# Revit family: Gira_537303
name_source: partatom
category: Electrical Fixtures
revit_build: Autodesk Revit 2017 (Build: 20160225_1515(x64)
units: mm (PartAtom-declared; Revit-internal decimal feet)

## family parameters
Cut with Voids When Loaded = No
Host = Face
Maintain Annotation Orientation = Yes
Part Type = Normal
Room Calculation Point = No
Round Connector Dimension = Use Diameter
Shared = No

## types (1)
- S3000 Beweg.m.aufs. 1,10 m Standard System 55 Reinweiß
    Ausführung = Bewegungsmelder
    Available = Yes
    Category = Bewegungsmelder-Sensor
    Data sheet (1) = https://katalog.gira.de
    Default Elevation = 1219 mm
    Farbe = weiß
    GTIN = 4010337049708
    Geeignet für Schutzart (IP) = IP22
    HAN = 537303
    Halogenfrei = Yes
    HeinzeBIM = https://bimportal.heinze.de
    Keynote = Bewegungsmelder_1,10m
    Manufacturer URL = https://www.gira.de
    Montageart = unter Putz
    Montagehöhe = 1,1 m
    Name = S3000 Beweg.m.aufs. 1,10 m Standard System 55 Reinweiß
    RAL-Nummer (ähnlich) = 9010
    Region = DE
    URL = http://katalog.gira.de
    Werkstoff = sonstige
    Werkstoffgüte = sonstige

## geometry (parser evidence)
native form markers: Blend x2, Sweep x3
no freeform markers — native parametric forms only
